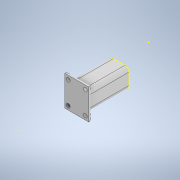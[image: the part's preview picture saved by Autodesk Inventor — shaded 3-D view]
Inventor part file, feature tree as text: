
AUTODESK INVENTOR PART (.ipt)
format: ipt  version: 2022 (Build 260153000, 153)  size: 458,240 bytes
history: native  units: in
note: dims shown in document units (in); Inventor stores cm internally (conversion verified against a paired STEP export)
features: projected_geometry x18, sketch x17, extrude x15, mirror x3, fillet x2
ambient origin geometry x8: Origin, YZ Plane, XZ Plane, XY Plane, X Axis, Y Axis, Z Axis, Center Point
bodies: Solid1 (feature_tree)
feature tree (55):
  extrude  "Extrusion1"  Depth=0.61in
  extrude  "Extrusion2"  Depth=2.5in TaperAngle=0.0deg
  extrude  "Extrusion3"  Depth=0.75in TaperAngle=0.0deg
  extrude  "Extrusion4"  Depth=2.25in
  sketch  "Sketch4"  dims[d5=0.18in d6=0.75in d7=0.0in]
  extrude  "Extrusion6"  Depth=0.8in
  extrude  "Extrusion7"  Depth=0.957in
  extrude  "Extrusion8"  Depth=0.157in
  mirror  "Mirror1"
  fillet  "Fillet4"  Radius=0.2362in
  sketch  "Sketch9"  dims[d17=0.195in d18=0.157in d19=0.2362in]
  extrude  "Extrusion9"  Depth=0.0984in
  extrude  "Extrusion10"  TaperAngle=0.0deg  [1 undecoded]
  extrude  "Extrusion11"  Depth=0.325in TaperAngle=0.0deg
  mirror  "Mirror2"
  extrude  "Extrusion12"  Depth=0.195in TaperAngle=0.0deg
  mirror  "Mirror3"
  sketch  "Sketch12"  dims[d25=1.5748in d28=0.325in d29=0.0in]
  sketch  "Sketch14"  dims[d30=1.0in d31=0.0in d32=0.195in d33=0.0in]
  extrude  "Extrusion14"  Depth=0.125in TaperAngle=0.0deg
  sketch  "Sketch16"  dims[d38=2.3in d39=0.0in d40=0.25in]
  sketch  "Sketch17"  dims[d41=0.157in d42=0.22in]
  extrude  "Extrusion16"  Depth=0.25in
  extrude  "Extrusion17"  Depth=0.22in
  sketch  "Sketch19"  dims[d47=0.1575in]
  extrude  "Extrusion18"  Depth=0.125in
  fillet  "Fillet5"  Radius=0.1575in
  sketch  "Sketch1"  dims[d0=0.61in d1=0.61in]
  sketch  "Sketch2"  dims[d2=0.61in d3=2.5in d4=0.0in]
  projected_geometry  "Projected Loop1"
  sketch  "Sketch5"  dims[d9=1.2in d10=2.25in]
  projected_geometry  "Projected Loop2"
  sketch  "Sketch6"  dims[d11=1.6in d12=0.8in]
  projected_geometry  "Projected Loop3"
  sketch  "Sketch7"  dims[d13=1.0in d14=0.0in d16=0.957in]
  projected_geometry  "Projected Loop4"
  projected_geometry  "Projected Loop5"
  sketch  "Sketch10"  dims[d20=0.0984in d21=0.0984in]
  sketch  "Sketch11"  dims[d22=2.25in d23=0.0in]
  projected_geometry  "Projected Loop6"
  projected_geometry  "Projected Loop7"
  sketch  "Sketch15"  dims[d35=0.125in d36=1.3in d37=0.0in]
  projected_geometry  "Projected Loop9"
  projected_geometry  "Projected Loop10"
  sketch  "Sketch18"  dims[d43=0.125in d44=0.0in d45=0.1575in d46=0.1575in]
  projected_geometry  "Projected Loop11"
  projected_geometry  "Projected Loop12"
  projected_geometry  "Projected Loop13"
  projected_geometry  "Projected Loop14"
  projected_geometry  "Projected Loop15"
  projected_geometry  "Projected Loop16"
  projected_geometry  "Projected Loop17"
  projected_geometry  "Projected Loop18"
  sketch  "Sketch20"  dims[d48=0.1575in d49=0.7425in d54=0.0394in d55=0.0in d56=0.6in d57=0.2125in d61=0.12in d62=0.12in d63=0.25in d64=0.0in d67=1.85in d68=0.0in d69=1.85in d70=0.0in d71=0.05in d72=0.0in d73=0.125in]
  projected_geometry  "Projected Loop19"
note: 1 required parameter value undecoded (feature->parameter linkage not recoverable at this tier; creation-order binding heuristic only, values carry confidence <= 0.55)
